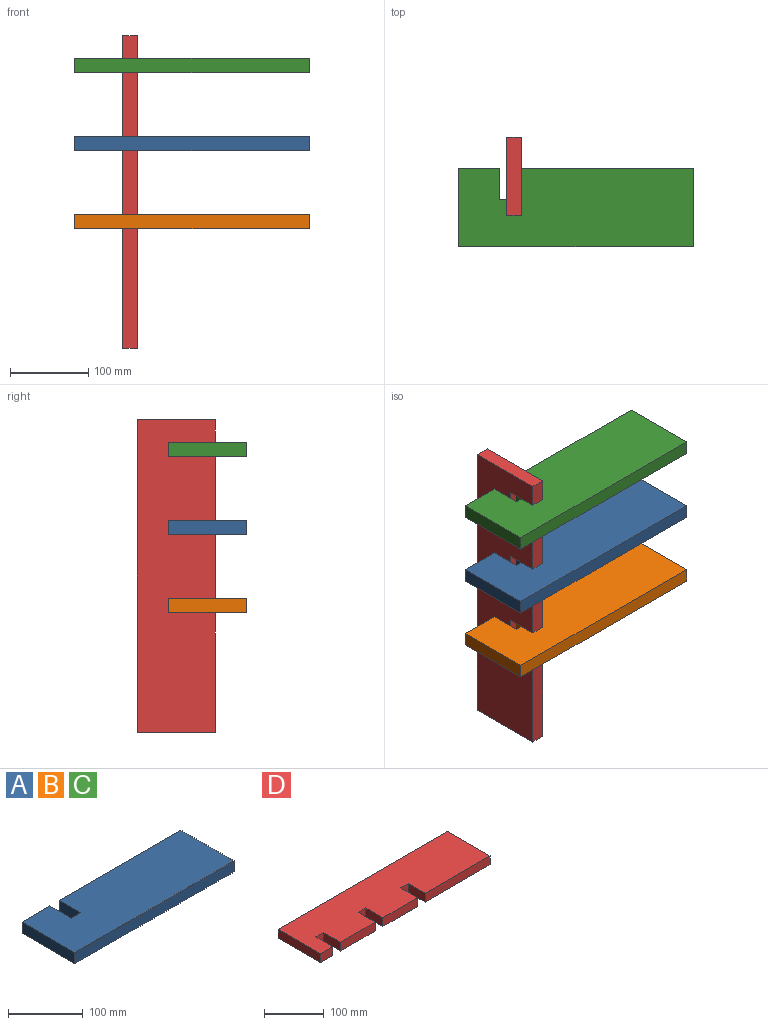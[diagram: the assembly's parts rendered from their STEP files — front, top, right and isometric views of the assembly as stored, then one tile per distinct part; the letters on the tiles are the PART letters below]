
ASSEMBLY  parts=4 mates=3
PART A: 10 faces, bbox 300x100x18 mm
  f0: plane 52.73x18mm, normal (0,1,0), area 949.1mm2, adj f1,f2,f3,f7
  f1: plane 300x100mm, normal (0,0,1), area 29280mm2, adj f0,f2,f4,f5,f6,f7,f8,f9
  f2: plane 100x18mm, normal (-1,0,0), area 1800mm2, adj f0,f1,f3,f5
  f3: plane 300x100mm, normal (0,0,-1), area 29280mm2, adj f0,f2,f4,f5,f6,f7,f8,f9
  f4: plane 100x18mm, normal (1,0,0), area 1800mm2, adj f1,f3,f5,f6
  f5: plane 300x18mm, normal (0,-1,0), area 5400mm2, adj f1,f2,f3,f4
  f6: plane 229.27x18mm, normal (0,1,0), area 4126.9mm2, adj f1,f3,f4,f9
  f7: plane 40x18mm, normal (1,0,0), area 720mm2, adj f0,f1,f3,f8
  f8: plane 18x18mm, normal (0,1,0), area 324mm2, adj f1,f3,f7,f9
  f9: plane 40x18mm, normal (-1,0,0), area 720mm2, adj f1,f3,f6,f8
PART B: same geometry as A
PART C: same geometry as A
PART D: 18 faces, bbox 400x100x18 mm
  f0: plane 40x18mm, normal (-1,0,0), area 720mm2, adj f1,f15,f16,f17
  f1: plane 152.79x18mm, normal (0,-1,0), area 2750.2mm2, adj f0,f2,f16,f17
  f2: plane 100x18mm, normal (1,0,0), area 1800mm2, adj f1,f3,f16,f17
  f3: plane 400x18mm, normal (0,1,0), area 7200mm2, adj f2,f4,f16,f17
  f4: plane 100x18mm, normal (-1,0,0), area 1800mm2, adj f3,f5,f16,f17
  f5: plane 29.21x18mm, normal (0,-1,0), area 525.8mm2, adj f4,f6,f16,f17
  f6: plane 40x18mm, normal (1,0,0), area 720mm2, adj f5,f7,f16,f17
  f7: plane 18x18mm, normal (0,-1,0), area 324mm2, adj f6,f8,f16,f17
  f8: plane 40x18mm, normal (-1,0,0), area 720mm2, adj f7,f9,f16,f17
  f9: plane 82x18mm, normal (0,-1,0), area 1476mm2, adj f8,f10,f16,f17
  f10: plane 40x18mm, normal (1,0,0), area 720mm2, adj f9,f11,f16,f17
  f11: plane 18x18mm, normal (0,-1,0), area 324mm2, adj f10,f12,f16,f17
  f12: plane 40x18mm, normal (-1,0,0), area 720mm2, adj f11,f13,f16,f17
  f13: plane 82x18mm, normal (0,-1,0), area 1476mm2, adj f12,f14,f16,f17
  f14: plane 40x18mm, normal (1,0,0), area 720mm2, adj f13,f15,f16,f17
  f15: plane 18x18mm, normal (0,-1,0), area 324mm2, adj f0,f14,f16,f17
  f16: plane 400x100mm, normal (0,0,1), area 37840mm2, adj f0,f1,f2,f3,f4,f5,f6,f7
  f17: plane 400x100mm, normal (0,0,-1), area 37840mm2, adj f0,f1,f2,f3,f4,f5,f6,f7
PLACE A rot(axis=(0,1,0),0deg) t=(10.4,12.07,51.65)mm
PLACE B rot(axis=(0.02,0.99,0.11),0deg) t=(10.4,12.07,-48.35)mm
PLACE C rot(axis=(0,1,0),0deg) t=(10.4,12.07,151.65)mm
PLACE D rot(axis=(0,1,0),90deg) t=(-141.44,7.82,-116.19)mm
MATE fastened B.f1 <-> D.f14  axis (0,0,1) through (-132.44,-27.93,-37.97)mm
MATE fastened C.f1 <-> D.f6  axis (0,0,1) through (-132.44,-27.93,162.03)mm
MATE fastened A.f1 <-> D.f10  axis (0,0,1) through (-132.44,-27.93,62.03)mm
